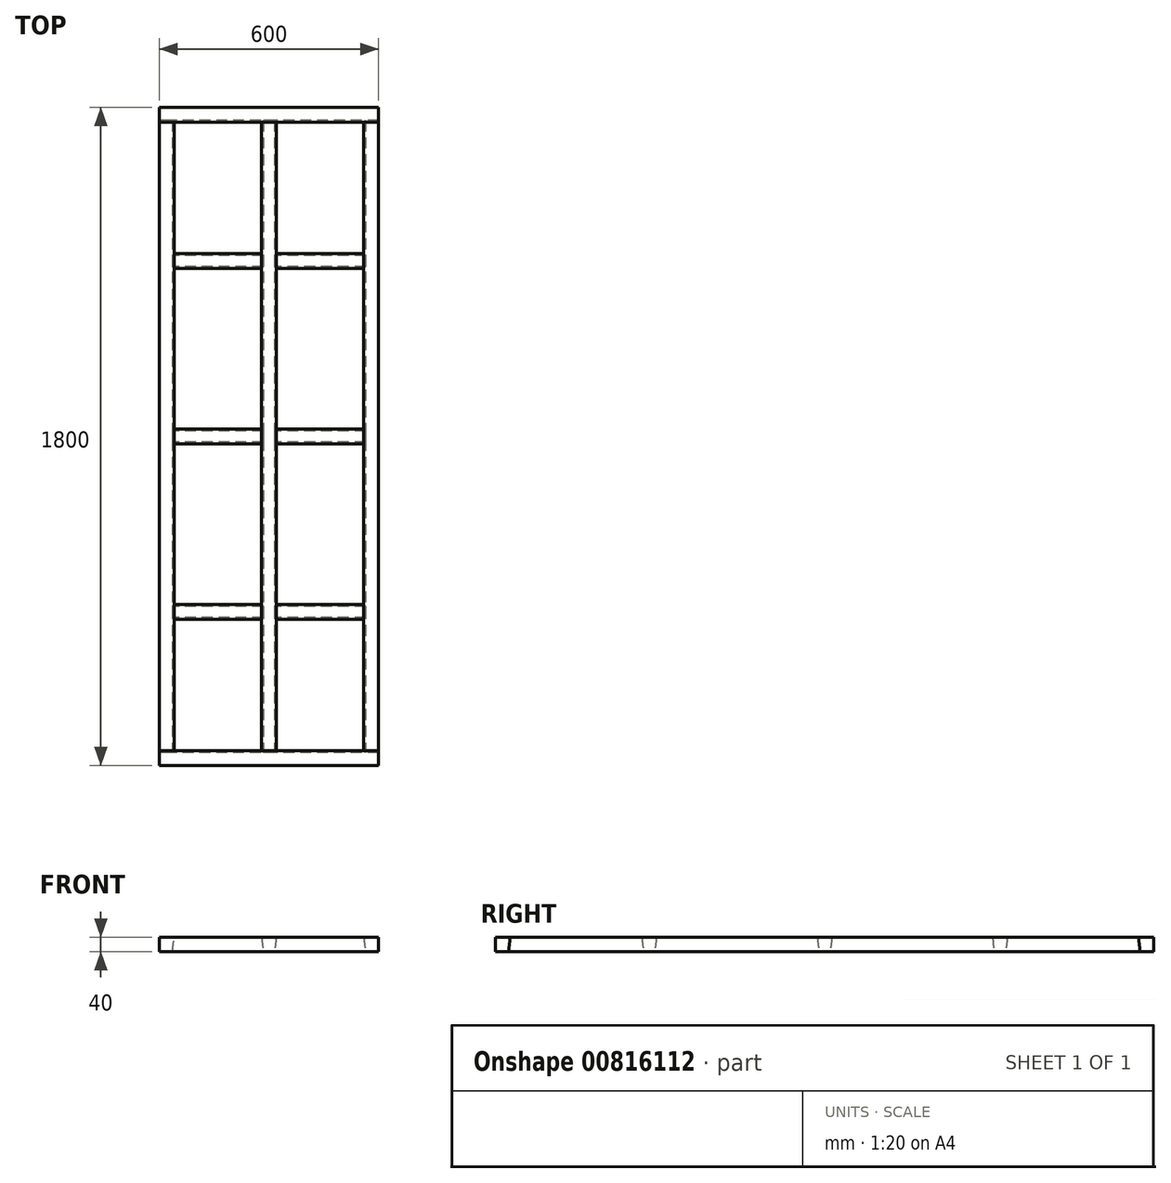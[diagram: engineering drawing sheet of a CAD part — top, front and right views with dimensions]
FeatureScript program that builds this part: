
annotation { "Feature Type Name" : "Feature", "Feature Type Description" : "" }
export const myFeature = defineFeature(function(context is Context, id is Id, definition is map)
    precondition{}
    {
        {
            var Q0;
            Q0=qCreatedBy(makeId("Front.planeOp"),FACE);
            var sketch = newSketch(context, id + "F0", { "sketchPlane" : qUnion([Q0])});
            skLineSegment(sketch, "E0", {"start": v(-170.34, 259.45) * mm, "end": v(-170.34, 254.45) * mm});
            skLineSegment(sketch, "E1.0", {"start": v(129.66, 259.45) * mm, "end": v(129.66, 254.45) * mm});
            skLineSegment(sketch, "E2", {"start": v(-170.34, 254.45) * mm, "end": v(-130.34, 254.45) * mm});
            skLineSegment(sketch, "E3", {"start": v(-125.34, 294.45) * mm, "end": v(104.66, 294.45) * mm});
            skLineSegment(sketch, "E4", {"start": v(109.66, 254.45) * mm, "end": v(129.66, 254.45) * mm});
            skLineSegment(sketch, "E5", {"start": v(-130.34, 254.45) * mm, "end": v(-125.34, 294.45) * mm});
            skLineSegment(sketch, "E6", {"start": v(104.66, 294.45) * mm, "end": v(109.66, 254.45) * mm});
            skLineSegment(sketch, "E7.1", {"start": v(-170.34, 259.45) * mm, "end": v(-134.75, 259.45) * mm});
            skLineSegment(sketch, "E8.1", {"start": v(-134.75, 259.45) * mm, "end": v(-129.75, 299.45) * mm});
            skLineSegment(sketch, "E9.0", {"start": v(114.08, 259.45) * mm, "end": v(129.66, 259.45) * mm});
            skLineSegment(sketch, "E9.1", {"start": v(109.08, 299.45) * mm, "end": v(114.08, 259.45) * mm});
            skLineSegment(sketch, "E9.2", {"start": v(-129.75, 299.45) * mm, "end": v(109.08, 299.45) * mm});
            skLineSegment(sketch, "E10.MirrorCS", {"start": v(149.66, 254.45) * mm, "end": v(129.66, 254.45) * mm});
            skLineSegment(sketch, "E11.MirrorCS", {"start": v(145.25, 259.45) * mm, "end": v(129.66, 259.45) * mm});
            skLineSegment(sketch, "E12.MirrorCS", {"start": v(150.25, 299.45) * mm, "end": v(145.25, 259.45) * mm});
            skLineSegment(sketch, "E13.MirrorCS", {"start": v(154.66, 294.45) * mm, "end": v(149.66, 254.45) * mm});
            skLineSegment(sketch, "E14.MirrorCS", {"start": v(389.08, 299.45) * mm, "end": v(150.25, 299.45) * mm});
            skLineSegment(sketch, "E15.MirrorCS", {"start": v(384.66, 294.45) * mm, "end": v(154.66, 294.45) * mm});
            skLineSegment(sketch, "E16.MirrorCS", {"start": v(394.08, 259.45) * mm, "end": v(389.08, 299.45) * mm});
            skLineSegment(sketch, "E17.MirrorCS", {"start": v(389.66, 254.45) * mm, "end": v(384.66, 294.45) * mm});
            skLineSegment(sketch, "E18.MirrorCS", {"start": v(429.66, 254.45) * mm, "end": v(389.66, 254.45) * mm});
            skLineSegment(sketch, "E19.MirrorCS", {"start": v(429.66, 259.45) * mm, "end": v(429.66, 254.45) * mm});
            skLineSegment(sketch, "E20.MirrorCS", {"start": v(429.66, 259.45) * mm, "end": v(394.08, 259.45) * mm});
            skLineSegment(sketch, "E21", {"start": v(-170.34, 254.45) * mm, "end": v(-170.34, 299.45) * mm});
            skLineSegment(sketch, "E22", {"start": v(-170.34, 299.45) * mm, "end": v(-129.75, 299.45) * mm});
            skLineSegment(sketch, "E23", {"start": v(114.08, 259.45) * mm, "end": v(145.25, 259.45) * mm});
            skLineSegment(sketch, "E24", {"start": v(109.08, 299.45) * mm, "end": v(150.25, 299.45) * mm});
            skLineSegment(sketch, "E25", {"start": v(389.08, 299.45) * mm, "end": v(429.66, 299.45) * mm});
            skLineSegment(sketch, "E26", {"start": v(429.66, 299.45) * mm, "end": v(429.66, 259.45) * mm});
            skSolve(sketch);
        }
        {
            var Q0;
            Q0=qSketchRegion(id+"F0",true);
            extrude(context, id + "F1", {"entities" : qUnion([Q0]), "oppositeDirection" : true, "depth" : 1800 * mm, "offsetDistance" : 25 * mm});
        }
        {
            var Q0;
            Q0=makeQuery(id+"F1.opExtrude","SWEPT_FACE",FACE,{"disambiguationData":[OSD([sQuery(id+"F0.wireOp",EDGE,"E21")])]});
            var sketch = newSketch(context, id + "F2", { "sketchPlane" : qUnion([Q0])});
            skLineSegment(sketch, "E27", {"start": v(0, 254.45) * mm, "end": v(0, 299.45) * mm});
            skLineSegment(sketch, "E28", {"start": v(-900, 299.45) * mm, "end": v(0, 299.45) * mm});
            skLineSegment(sketch, "E29.0", {"start": v(-880.04, 294.45) * mm, "end": v(-439.96, 294.45) * mm});
            skLineSegment(sketch, "E30", {"start": v(-900, 254.45) * mm, "end": v(0, 254.45) * mm});
            skLineSegment(sketch, "E31.0", {"start": v(-900, 259.45) * mm, "end": v(-884.41, 259.45) * mm});
            skLineSegment(sketch, "E32", {"start": v(-40, 254.45) * mm, "end": v(-45, 294.45) * mm});
            skLineSegment(sketch, "E33", {"start": v(-400, 254.45) * mm, "end": v(-395, 294.45) * mm});
            skLineSegment(sketch, "E34", {"start": v(-440, 254.45) * mm, "end": v(-445, 294.45) * mm});
            skLineSegment(sketch, "E35", {"start": v(-880, 254.45) * mm, "end": v(-875, 294.45) * mm});
            skLineSegment(sketch, "E36.0", {"start": v(-884.41, 259.45) * mm, "end": v(-879.41, 299.45) * mm});
            skLineSegment(sketch, "E37.trimOffspring", {"start": v(-879.37, 259.45) * mm, "end": v(-440.62, 259.45) * mm});
            skLineSegment(sketch, "E38.0", {"start": v(-404.41, 259.45) * mm, "end": v(-399.41, 299.45) * mm});
            skLineSegment(sketch, "E39.0", {"start": v(-435.59, 259.45) * mm, "end": v(-440.59, 299.45) * mm});
            skLineSegment(sketch, "E40.trimOffspring", {"start": v(-400.04, 294.45) * mm, "end": v(-39.96, 294.45) * mm});
            skLineSegment(sketch, "E41.0", {"start": v(-35.59, 259.45) * mm, "end": v(-40.59, 299.45) * mm});
            skLineSegment(sketch, "E42.trimOffspring", {"start": v(-35.59, 259.45) * mm, "end": v(0, 259.45) * mm});
            skLineSegment(sketch, "E43.trimOffspring", {"start": v(-399.38, 259.45) * mm, "end": v(-40.63, 259.45) * mm});
            skLineSegment(sketch, "E44.trimOffspring", {"start": v(-435.59, 259.45) * mm, "end": v(-404.41, 259.45) * mm});
            skLineSegment(sketch, "E45.MirrorCS", {"start": v(-900, 259.45) * mm, "end": v(-915.59, 259.45) * mm});
            skLineSegment(sketch, "E46.MirrorCS", {"start": v(-900, 254.45) * mm, "end": v(-1800, 254.45) * mm});
            skLineSegment(sketch, "E47.MirrorCS", {"start": v(-915.59, 259.45) * mm, "end": v(-920.59, 299.45) * mm});
            skLineSegment(sketch, "E48.MirrorCS", {"start": v(-920, 254.45) * mm, "end": v(-925, 294.45) * mm});
            skLineSegment(sketch, "E49.MirrorCS", {"start": v(-919.96, 294.45) * mm, "end": v(-1360.04, 294.45) * mm});
            skLineSegment(sketch, "E50.MirrorCS", {"start": v(-900, 299.45) * mm, "end": v(-1800, 299.45) * mm});
            skLineSegment(sketch, "E51.MirrorCS", {"start": v(-1364.41, 259.45) * mm, "end": v(-1395.59, 259.45) * mm});
            skLineSegment(sketch, "E52.MirrorCS", {"start": v(-1364.41, 259.45) * mm, "end": v(-1359.41, 299.45) * mm});
            skLineSegment(sketch, "E53.MirrorCS", {"start": v(-1395.59, 259.45) * mm, "end": v(-1400.59, 299.45) * mm});
            skLineSegment(sketch, "E54.MirrorCS", {"start": v(-1360, 254.45) * mm, "end": v(-1355, 294.45) * mm});
            skLineSegment(sketch, "E55.MirrorCS", {"start": v(-1400, 254.45) * mm, "end": v(-1405, 294.45) * mm});
            skLineSegment(sketch, "E56.MirrorCS", {"start": v(-1399.96, 294.45) * mm, "end": v(-1760.04, 294.45) * mm});
            skLineSegment(sketch, "E57.MirrorCS", {"start": v(-1400.63, 259.45) * mm, "end": v(-1759.38, 259.45) * mm});
            skLineSegment(sketch, "E58.MirrorCS", {"start": v(-1764.41, 259.45) * mm, "end": v(-1759.41, 299.45) * mm});
            skLineSegment(sketch, "E59.MirrorCS", {"start": v(-1760, 254.45) * mm, "end": v(-1755, 294.45) * mm});
            skLineSegment(sketch, "E60.MirrorCS", {"start": v(-1764.41, 259.45) * mm, "end": v(-1800, 259.45) * mm});
            skLineSegment(sketch, "E61.MirrorCS", {"start": v(-1800, 254.45) * mm, "end": v(-1800, 299.45) * mm});
            skSolve(sketch);
        }
        {
            var Q0;
            {var subQ0=sQuery(id+"F2.wireOp",EDGE,"E60.MirrorCS");Q0=makeQuery(id+"F2.imprint","IMPRINT",FACE,{"disambiguationData":[TD([[makeQuery(id+"F2.imprint","IMPRINT",EDGE,{"derivedFrom":subQ0}),1.0]])]});}
            extrude(context, id + "F3", {"entities" : qUnion([Q0]), "operationType" : NewBodyOperationType.REMOVE, "oppositeDirection" : true, "depth" : 800 * mm, "offsetDistance" : 25 * mm});
        }
        {
            var Q0;
            {var subQ0=sQuery(id+"F2.wireOp",EDGE,"E60.MirrorCS");Q0=makeQuery(id+"F2.imprint","IMPRINT",FACE,{"disambiguationData":[TD([[makeQuery(id+"F2.imprint","IMPRINT",EDGE,{"derivedFrom":subQ0}),-1.0]])]});}
            extrude(context, id + "F4", {"entities" : qUnion([Q0]), "operationType" : NewBodyOperationType.ADD, "oppositeDirection" : true, "depth" : 600 * mm, "offsetDistance" : 25 * mm});
        }
        {
            var Q0;
            {var subQ0=sQuery(id+"F2.wireOp",EDGE,"E58.MirrorCS");var subQ1=sQuery(id+"F2.wireOp",EDGE,"E56.MirrorCS");var subQ2=makeQuery(id+"F2.imprint","INTERSECT",VERTEX,{"derivedFrom":[subQ1,subQ0]});Q0=makeQuery(id+"F2.imprint","IMPRINT",FACE,{"disambiguationData":[TD([[makeQuery(id+"F2.imprint","IMPRINT",EDGE,{"disambiguationData":[TD([[subQ2,1.0]])],"derivedFrom":subQ1}),1.0]])]});}
            extrude(context, id + "F5", {"entities" : qUnion([Q0]), "operationType" : NewBodyOperationType.ADD, "oppositeDirection" : true, "depth" : 600 * mm, "offsetDistance" : 25 * mm});
        }
        {
            var Q0;
            {var subQ1=sQuery(id+"F2.wireOp",EDGE,"E51.MirrorCS");Q0=makeQuery(id+"F2.imprint","IMPRINT",FACE,{"disambiguationData":[TD([[makeQuery(id+"F2.imprint","IMPRINT",EDGE,{"derivedFrom":subQ1}),1.0]])]});}
            var Q1;
            {var subQ2=sQuery(id+"F2.wireOp",EDGE,"E31.0");Q1=makeQuery(id+"F2.imprint","IMPRINT",FACE,{"disambiguationData":[TD([[makeQuery(id+"F2.imprint","IMPRINT",EDGE,{"derivedFrom":subQ2}),1.0]])]});}
            var Q2;
            {var subQ1=sQuery(id+"F2.wireOp",EDGE,"E45.MirrorCS");Q2=makeQuery(id+"F2.imprint","IMPRINT",FACE,{"disambiguationData":[TD([[makeQuery(id+"F2.imprint","IMPRINT",EDGE,{"derivedFrom":subQ1}),1.0]])]});}
            var Q3;
            {var subQ4=sQuery(id+"F2.wireOp",EDGE,"E44.trimOffspring");Q3=makeQuery(id+"F2.imprint","IMPRINT",FACE,{"disambiguationData":[TD([[makeQuery(id+"F2.imprint","IMPRINT",EDGE,{"derivedFrom":subQ4}),1.0]])]});}
            var Q4;
            {var subQ6=sQuery(id+"F2.wireOp",EDGE,"E42.trimOffspring");Q4=makeQuery(id+"F2.imprint","IMPRINT",FACE,{"disambiguationData":[TD([[makeQuery(id+"F2.imprint","IMPRINT",EDGE,{"derivedFrom":subQ6}),1.0]])]});}
            extrude(context, id + "F6", {"entities" : qUnion([Q0, Q1, Q2, Q3, Q4]), "operationType" : NewBodyOperationType.REMOVE, "oppositeDirection" : true, "depth" : 800 * mm, "offsetDistance" : 25 * mm});
        }
        {
            var Q0;
            {var subQ0=sQuery(id+"F2.wireOp",EDGE,"E40.trimOffspring");var subQ1=sQuery(id+"F2.wireOp",EDGE,"E32");var subQ2=makeQuery(id+"F2.imprint","INTERSECT",VERTEX,{"derivedFrom":[subQ1,subQ0]});Q0=makeQuery(id+"F2.imprint","IMPRINT",FACE,{"disambiguationData":[TD([[makeQuery(id+"F2.imprint","IMPRINT",EDGE,{"disambiguationData":[TD([[subQ2,-1.0]])],"derivedFrom":subQ0}),-1.0]])]});}
            var Q1;
            {var subQ0=sQuery(id+"F2.wireOp",EDGE,"E42.trimOffspring");Q1=makeQuery(id+"F2.imprint","IMPRINT",FACE,{"disambiguationData":[TD([[makeQuery(id+"F2.imprint","IMPRINT",EDGE,{"derivedFrom":subQ0}),-1.0]])]});}
            var Q2;
            {var subQ0=sQuery(id+"F2.wireOp",EDGE,"E39.0");var subQ1=sQuery(id+"F2.wireOp",EDGE,"E29.0");var subQ2=makeQuery(id+"F2.imprint","INTERSECT",VERTEX,{"derivedFrom":[subQ1,subQ0]});Q2=makeQuery(id+"F2.imprint","IMPRINT",FACE,{"disambiguationData":[TD([[makeQuery(id+"F2.imprint","IMPRINT",EDGE,{"disambiguationData":[TD([[subQ2,1.0]])],"derivedFrom":subQ1}),-1.0]])]});}
            var Q3;
            {var subQ5=sQuery(id+"F2.wireOp",EDGE,"E44.trimOffspring");Q3=makeQuery(id+"F2.imprint","IMPRINT",FACE,{"disambiguationData":[TD([[makeQuery(id+"F2.imprint","IMPRINT",EDGE,{"derivedFrom":subQ5}),-1.0]])]});}
            var Q4;
            {var subQ0=sQuery(id+"F2.wireOp",EDGE,"E40.trimOffspring");var subQ1=sQuery(id+"F2.wireOp",EDGE,"E33");var subQ2=makeQuery(id+"F2.imprint","INTERSECT",VERTEX,{"derivedFrom":[subQ1,subQ0]});Q4=makeQuery(id+"F2.imprint","IMPRINT",FACE,{"disambiguationData":[TD([[makeQuery(id+"F2.imprint","IMPRINT",EDGE,{"disambiguationData":[TD([[subQ2,1.0]])],"derivedFrom":subQ0}),-1.0]])]});}
            var Q5;
            {var subQ3=sQuery(id+"F2.wireOp",EDGE,"E49.MirrorCS");var subQ5=sQuery(id+"F2.wireOp",EDGE,"E48.MirrorCS");var subQ6=makeQuery(id+"F2.imprint","INTERSECT",VERTEX,{"derivedFrom":[subQ5,subQ3]});Q5=makeQuery(id+"F2.imprint","IMPRINT",FACE,{"disambiguationData":[TD([[makeQuery(id+"F2.imprint","IMPRINT",EDGE,{"disambiguationData":[TD([[subQ6,1.0]])],"derivedFrom":subQ3}),1.0]])]});}
            var Q6;
            {var subQ7=sQuery(id+"F2.wireOp",EDGE,"E45.MirrorCS");Q6=makeQuery(id+"F2.imprint","IMPRINT",FACE,{"disambiguationData":[TD([[makeQuery(id+"F2.imprint","IMPRINT",EDGE,{"derivedFrom":subQ7}),-1.0]])]});}
            var Q7;
            {var subQ7=sQuery(id+"F2.wireOp",EDGE,"E31.0");Q7=makeQuery(id+"F2.imprint","IMPRINT",FACE,{"disambiguationData":[TD([[makeQuery(id+"F2.imprint","IMPRINT",EDGE,{"derivedFrom":subQ7}),-1.0]])]});}
            var Q8;
            {var subQ0=sQuery(id+"F2.wireOp",EDGE,"E36.0");var subQ1=sQuery(id+"F2.wireOp",EDGE,"E29.0");var subQ2=makeQuery(id+"F2.imprint","INTERSECT",VERTEX,{"derivedFrom":[subQ1,subQ0]});Q8=makeQuery(id+"F2.imprint","IMPRINT",FACE,{"disambiguationData":[TD([[makeQuery(id+"F2.imprint","IMPRINT",EDGE,{"disambiguationData":[TD([[subQ2,-1.0]])],"derivedFrom":subQ1}),-1.0]])]});}
            var Q9;
            {var subQ3=sQuery(id+"F2.wireOp",EDGE,"E56.MirrorCS");var subQ5=sQuery(id+"F2.wireOp",EDGE,"E55.MirrorCS");var subQ6=makeQuery(id+"F2.imprint","INTERSECT",VERTEX,{"derivedFrom":[subQ5,subQ3]});Q9=makeQuery(id+"F2.imprint","IMPRINT",FACE,{"disambiguationData":[TD([[makeQuery(id+"F2.imprint","IMPRINT",EDGE,{"disambiguationData":[TD([[subQ6,1.0]])],"derivedFrom":subQ3}),1.0]])]});}
            var Q10;
            {var subQ5=sQuery(id+"F2.wireOp",EDGE,"E51.MirrorCS");Q10=makeQuery(id+"F2.imprint","IMPRINT",FACE,{"disambiguationData":[TD([[makeQuery(id+"F2.imprint","IMPRINT",EDGE,{"derivedFrom":subQ5}),-1.0]])]});}
            var Q11;
            {var subQ0=sQuery(id+"F2.wireOp",EDGE,"E52.MirrorCS");var subQ1=sQuery(id+"F2.wireOp",EDGE,"E49.MirrorCS");var subQ2=makeQuery(id+"F2.imprint","INTERSECT",VERTEX,{"derivedFrom":[subQ1,subQ0]});Q11=makeQuery(id+"F2.imprint","IMPRINT",FACE,{"disambiguationData":[TD([[makeQuery(id+"F2.imprint","IMPRINT",EDGE,{"disambiguationData":[TD([[subQ2,1.0]])],"derivedFrom":subQ1}),1.0]])]});}
            extrude(context, id + "F7", {"entities" : qUnion([Q0, Q1, Q2, Q3, Q4, Q5, Q6, Q7, Q8, Q9, Q10, Q11]), "operationType" : NewBodyOperationType.ADD, "oppositeDirection" : true, "depth" : 600 * mm, "offsetDistance" : 25 * mm});
        }
        {
            var Q0;
            {var subQ0=sQuery(id+"F0.wireOp",EDGE,"E7.1");Q0=makeQuery(id+"F0.imprint","IMPRINT",FACE,{"disambiguationData":[TD([[makeQuery(id+"F0.imprint","IMPRINT",EDGE,{"derivedFrom":subQ0}),1.0]])]});}
            extrude(context, id + "F8", {"entities" : qUnion([Q0]), "operationType" : NewBodyOperationType.REMOVE, "oppositeDirection" : true, "depth" : 1900 * mm, "offsetDistance" : 25 * mm});
        }
        {
            var Q0;
            {var subQ3=sQuery(id+"F0.wireOp",EDGE,"E9.1");Q0=makeQuery(id+"F0.imprint","IMPRINT",FACE,{"disambiguationData":[TD([[makeQuery(id+"F0.imprint","IMPRINT",EDGE,{"derivedFrom":subQ3}),1.0]])]});}
            extrude(context, id + "F9", {"entities" : qUnion([Q0]), "operationType" : NewBodyOperationType.REMOVE, "oppositeDirection" : true, "depth" : 1900 * mm, "offsetDistance" : 25 * mm});
        }
        {
            var Q0;
            Q0=makeQuery(id+"F0.imprint","IMPRINT",FACE,{"disambiguationData":[TD([[makeQuery(id+"F0.imprint","IMPRINT",EDGE,{"derivedFrom":sQuery(id+"F0.wireOp",EDGE,"E16.MirrorCS")}),-1.0]])]});
            extrude(context, id + "F10", {"entities" : qUnion([Q0]), "operationType" : NewBodyOperationType.REMOVE, "oppositeDirection" : true, "depth" : 1900 * mm, "offsetDistance" : 25 * mm});
        }
        {
            var Q0;
            {var subQ4=sQuery(id+"F2.wireOp",EDGE,"E60.MirrorCS");Q0=makeQuery(id+"F2.imprint","IMPRINT",FACE,{"disambiguationData":[TD([[makeQuery(id+"F2.imprint","IMPRINT",EDGE,{"derivedFrom":subQ4}),-1.0]])]});}
            var Q1;
            {var subQ1=sQuery(id+"F2.wireOp",EDGE,"E51.MirrorCS");Q1=makeQuery(id+"F2.imprint","IMPRINT",FACE,{"disambiguationData":[TD([[makeQuery(id+"F2.imprint","IMPRINT",EDGE,{"derivedFrom":subQ1}),-1.0]])]});}
            var Q2;
            {var subQ1=sQuery(id+"F2.wireOp",EDGE,"E45.MirrorCS");Q2=makeQuery(id+"F2.imprint","IMPRINT",FACE,{"disambiguationData":[TD([[makeQuery(id+"F2.imprint","IMPRINT",EDGE,{"derivedFrom":subQ1}),-1.0]])]});}
            extrude(context, id + "F11", {"entities" : qUnion([Q0, Q1, Q2]), "operationType" : NewBodyOperationType.REMOVE, "oppositeDirection" : true, "depth" : 800 * mm, "offsetDistance" : 25 * mm});
        }
        {
            var Q0;
            {var subQ0=sQuery(id+"F0.wireOp",EDGE,"E7.1");Q0=makeQuery(id+"F0.imprint","IMPRINT",FACE,{"disambiguationData":[TD([[makeQuery(id+"F0.imprint","IMPRINT",EDGE,{"derivedFrom":subQ0}),1.0]])]});}
            var Q1;
            {var subQ3=sQuery(id+"F0.wireOp",EDGE,"E9.1");Q1=makeQuery(id+"F0.imprint","IMPRINT",FACE,{"disambiguationData":[TD([[makeQuery(id+"F0.imprint","IMPRINT",EDGE,{"derivedFrom":subQ3}),1.0]])]});}
            var Q2;
            Q2=makeQuery(id+"F0.imprint","IMPRINT",FACE,{"disambiguationData":[TD([[makeQuery(id+"F0.imprint","IMPRINT",EDGE,{"derivedFrom":sQuery(id+"F0.wireOp",EDGE,"E16.MirrorCS")}),-1.0]])]});
            extrude(context, id + "F12", {"entities" : qUnion([Q0, Q1, Q2]), "oppositeDirection" : true, "depth" : 1800 * mm, "offsetDistance" : 25 * mm});
        }
        {
            var Q0;
            {var subQ4=sQuery(id+"F2.wireOp",EDGE,"E60.MirrorCS");Q0=makeQuery(id+"F2.imprint","IMPRINT",FACE,{"disambiguationData":[TD([[makeQuery(id+"F2.imprint","IMPRINT",EDGE,{"derivedFrom":subQ4}),-1.0]])]});}
            var Q1;
            {var subQ1=sQuery(id+"F2.wireOp",EDGE,"E51.MirrorCS");Q1=makeQuery(id+"F2.imprint","IMPRINT",FACE,{"disambiguationData":[TD([[makeQuery(id+"F2.imprint","IMPRINT",EDGE,{"derivedFrom":subQ1}),-1.0]])]});}
            var Q2;
            {var subQ2=sQuery(id+"F2.wireOp",EDGE,"E31.0");Q2=makeQuery(id+"F2.imprint","IMPRINT",FACE,{"disambiguationData":[TD([[makeQuery(id+"F2.imprint","IMPRINT",EDGE,{"derivedFrom":subQ2}),1.0]])]});}
            var Q3;
            {var subQ4=sQuery(id+"F2.wireOp",EDGE,"E44.trimOffspring");Q3=makeQuery(id+"F2.imprint","IMPRINT",FACE,{"disambiguationData":[TD([[makeQuery(id+"F2.imprint","IMPRINT",EDGE,{"derivedFrom":subQ4}),1.0]])]});}
            var Q4;
            {var subQ4=sQuery(id+"F2.wireOp",EDGE,"E42.trimOffspring");Q4=makeQuery(id+"F2.imprint","IMPRINT",FACE,{"disambiguationData":[TD([[makeQuery(id+"F2.imprint","IMPRINT",EDGE,{"derivedFrom":subQ4}),1.0]])]});}
            extrude(context, id + "F13", {"entities" : qUnion([Q0, Q1, Q2, Q3, Q4]), "oppositeDirection" : true, "depth" : 600 * mm, "offsetDistance" : 25 * mm});
        }
        {
            var Q0;
            Q0=makeQuery(id+"F12.opExtrude","SWEPT_BODY",BODY,{"disambiguationData":[OSD([sQuery(id+"F0.wireOp",EDGE,"E16.MirrorCS"),sQuery(id+"F0.wireOp",EDGE,"E20.MirrorCS"),sQuery(id+"F0.wireOp",EDGE,"E25"),sQuery(id+"F0.wireOp",EDGE,"E26")])]});
            var Q1;
            Q1=makeQuery(id+"F12.opExtrude","SWEPT_BODY",BODY,{"disambiguationData":[OSD([sQuery(id+"F0.wireOp",EDGE,"E9.1"),sQuery(id+"F0.wireOp",EDGE,"E12.MirrorCS"),sQuery(id+"F0.wireOp",EDGE,"E23"),sQuery(id+"F0.wireOp",EDGE,"E24")])]});
            var Q2;
            Q2=makeQuery(id+"F12.opExtrude","SWEPT_BODY",BODY,{"disambiguationData":[OSD([sQuery(id+"F0.wireOp",EDGE,"E7.1"),sQuery(id+"F0.wireOp",EDGE,"E8.1"),sQuery(id+"F0.wireOp",EDGE,"E21"),sQuery(id+"F0.wireOp",EDGE,"E22")])]});
            var Q3;
            Q3=makeQuery(id+"F13.opExtrude","SWEPT_BODY",BODY,{"disambiguationData":[OSD([sQuery(id+"F2.wireOp",EDGE,"E28"),sQuery(id+"F2.wireOp",EDGE,"E38.0"),sQuery(id+"F2.wireOp",EDGE,"E39.0"),sQuery(id+"F2.wireOp",EDGE,"E44.trimOffspring")])]});
            var Q4;
            Q4=makeQuery(id+"F13.opExtrude","SWEPT_BODY",BODY,{"disambiguationData":[OSD([sQuery(id+"F2.wireOp",EDGE,"E28"),sQuery(id+"F2.wireOp",EDGE,"E31.0"),sQuery(id+"F2.wireOp",EDGE,"E36.0"),sQuery(id+"F2.wireOp",EDGE,"E45.MirrorCS"),sQuery(id+"F2.wireOp",EDGE,"E47.MirrorCS"),sQuery(id+"F2.wireOp",EDGE,"E50.MirrorCS")])]});
            var Q5;
            Q5=makeQuery(id+"F13.opExtrude","SWEPT_BODY",BODY,{"disambiguationData":[OSD([sQuery(id+"F2.wireOp",EDGE,"E51.MirrorCS"),sQuery(id+"F2.wireOp",EDGE,"E52.MirrorCS"),sQuery(id+"F2.wireOp",EDGE,"E53.MirrorCS"),sQuery(id+"F2.wireOp",EDGE,"E50.MirrorCS")])]});
            booleanBodies(context, id + "F14", {"operationType" : BooleanOperationType.SUBTRACTION, "tools" : qUnion([Q0, Q1, Q2]), "targets" : qUnion([Q3, Q4, Q5]), "keepTools" : true});
        }
        {
            var Q0;
            Q0=makeQuery(id+"F13.opExtrude","SWEPT_BODY",BODY,{"disambiguationData":[OSD([sQuery(id+"F2.wireOp",EDGE,"E27"),sQuery(id+"F2.wireOp",EDGE,"E28"),sQuery(id+"F2.wireOp",EDGE,"E41.0"),sQuery(id+"F2.wireOp",EDGE,"E42.trimOffspring")])]});
            var Q1;
            Q1=makeQuery(id+"F6.boolean.opBoolean","SPLIT",BODY,{"disambiguationData":[OD(0.0)],"derivedFrom":makeQuery(id+"F1.opExtrude","SWEPT_BODY",BODY,{"disambiguationData":[OSD([sQuery(id+"F0.wireOp",EDGE,"E2"),sQuery(id+"F0.wireOp",EDGE,"E3"),sQuery(id+"F0.wireOp",EDGE,"E4"),sQuery(id+"F0.wireOp",EDGE,"E5"),sQuery(id+"F0.wireOp",EDGE,"E6"),sQuery(id+"F0.wireOp",EDGE,"E9.2"),sQuery(id+"F0.wireOp",EDGE,"E10.MirrorCS"),sQuery(id+"F0.wireOp",EDGE,"E13.MirrorCS"),sQuery(id+"F0.wireOp",EDGE,"E14.MirrorCS"),sQuery(id+"F0.wireOp",EDGE,"E15.MirrorCS"),sQuery(id+"F0.wireOp",EDGE,"E17.MirrorCS"),sQuery(id+"F0.wireOp",EDGE,"E18.MirrorCS"),sQuery(id+"F0.wireOp",EDGE,"E19.MirrorCS"),sQuery(id+"F0.wireOp",EDGE,"E21"),sQuery(id+"F0.wireOp",EDGE,"E22"),sQuery(id+"F0.wireOp",EDGE,"E24"),sQuery(id+"F0.wireOp",EDGE,"E25"),sQuery(id+"F0.wireOp",EDGE,"E26")])]})});
            var Q2;
            Q2=makeQuery(id+"F12.opExtrude","SWEPT_BODY",BODY,{"disambiguationData":[OSD([sQuery(id+"F0.wireOp",EDGE,"E9.1"),sQuery(id+"F0.wireOp",EDGE,"E12.MirrorCS"),sQuery(id+"F0.wireOp",EDGE,"E23"),sQuery(id+"F0.wireOp",EDGE,"E24")])]});
            booleanBodies(context, id + "F15", {"operationType" : BooleanOperationType.SUBTRACTION, "tools" : qUnion([Q0]), "targets" : qUnion([Q1, Q2]), "keepTools" : true});
        }
        {
            var Q0;
            Q0=makeQuery(id+"F13.opExtrude","SWEPT_BODY",BODY,{"disambiguationData":[OSD([sQuery(id+"F2.wireOp",EDGE,"E27"),sQuery(id+"F2.wireOp",EDGE,"E28"),sQuery(id+"F2.wireOp",EDGE,"E41.0"),sQuery(id+"F2.wireOp",EDGE,"E42.trimOffspring")])]});
            var Q1;
            Q1=makeQuery(id+"F13.opExtrude","SWEPT_BODY",BODY,{"disambiguationData":[OSD([sQuery(id+"F2.wireOp",EDGE,"E50.MirrorCS"),sQuery(id+"F2.wireOp",EDGE,"E58.MirrorCS"),sQuery(id+"F2.wireOp",EDGE,"E60.MirrorCS"),sQuery(id+"F2.wireOp",EDGE,"E61.MirrorCS")])]});
            var Q2;
            Q2=makeQuery(id+"F12.opExtrude","SWEPT_BODY",BODY,{"disambiguationData":[OSD([sQuery(id+"F0.wireOp",EDGE,"E16.MirrorCS"),sQuery(id+"F0.wireOp",EDGE,"E20.MirrorCS"),sQuery(id+"F0.wireOp",EDGE,"E25"),sQuery(id+"F0.wireOp",EDGE,"E26")])]});
            var Q3;
            Q3=makeQuery(id+"F12.opExtrude","SWEPT_BODY",BODY,{"disambiguationData":[OSD([sQuery(id+"F0.wireOp",EDGE,"E9.1"),sQuery(id+"F0.wireOp",EDGE,"E12.MirrorCS"),sQuery(id+"F0.wireOp",EDGE,"E23"),sQuery(id+"F0.wireOp",EDGE,"E24")])]});
            var Q4;
            Q4=makeQuery(id+"F12.opExtrude","SWEPT_BODY",BODY,{"disambiguationData":[OSD([sQuery(id+"F0.wireOp",EDGE,"E7.1"),sQuery(id+"F0.wireOp",EDGE,"E8.1"),sQuery(id+"F0.wireOp",EDGE,"E21"),sQuery(id+"F0.wireOp",EDGE,"E22")])]});
            booleanBodies(context, id + "F16", {"operationType" : BooleanOperationType.SUBTRACTION, "tools" : qUnion([Q0, Q1]), "targets" : qUnion([Q2, Q3, Q4]), "keepTools" : true});
        }
        {
            var Q0;
            Q0=makeQuery(id+"F6.boolean.opBoolean","SPLIT",BODY,{"disambiguationData":[OD(0.0)],"derivedFrom":makeQuery(id+"F1.opExtrude","SWEPT_BODY",BODY,{"disambiguationData":[OSD([sQuery(id+"F0.wireOp",EDGE,"E2"),sQuery(id+"F0.wireOp",EDGE,"E3"),sQuery(id+"F0.wireOp",EDGE,"E4"),sQuery(id+"F0.wireOp",EDGE,"E5"),sQuery(id+"F0.wireOp",EDGE,"E6"),sQuery(id+"F0.wireOp",EDGE,"E9.2"),sQuery(id+"F0.wireOp",EDGE,"E10.MirrorCS"),sQuery(id+"F0.wireOp",EDGE,"E13.MirrorCS"),sQuery(id+"F0.wireOp",EDGE,"E14.MirrorCS"),sQuery(id+"F0.wireOp",EDGE,"E15.MirrorCS"),sQuery(id+"F0.wireOp",EDGE,"E17.MirrorCS"),sQuery(id+"F0.wireOp",EDGE,"E18.MirrorCS"),sQuery(id+"F0.wireOp",EDGE,"E19.MirrorCS"),sQuery(id+"F0.wireOp",EDGE,"E21"),sQuery(id+"F0.wireOp",EDGE,"E22"),sQuery(id+"F0.wireOp",EDGE,"E24"),sQuery(id+"F0.wireOp",EDGE,"E25"),sQuery(id+"F0.wireOp",EDGE,"E26")])]})});
            deleteBodies(context, id + "F17", {"entities" : qUnion([Q0])});
        }
    });
